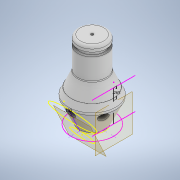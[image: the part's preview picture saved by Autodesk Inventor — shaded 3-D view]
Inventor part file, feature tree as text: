
AUTODESK INVENTOR PART (.ipt)
format: ipt  version: 2020 (Build 240168000, 168)  size: 301,056 bytes
history: native  units: in
note: dims shown in document units (in); Inventor stores cm internally (conversion verified against a paired STEP export)
features: sketch x6, hole x4, plane x2, fillet x2, revolve x1, pattern_circular x1
ambient origin geometry x8: Origin, YZ Plane, XZ Plane, XY Plane, X Axis, Y Axis, Z Axis, Center Point
bodies: Solid1 (feature_tree)
feature tree (16):
  revolve  "Revolution1"  [1 undecoded]
  hole  "Hole4"  [1 undecoded]
  hole  "Hole8"  [1 undecoded]
  sketch  "Sketch13"  dims[d2=90.0deg d3=0.057in]
  plane  "Work Plane6"
  sketch  "Sketch14"  dims[d4=0.095in d5=0.125in]
  sketch  "Sketch29"  dims[d24=0.4466in d25=0.125in]
  plane  "Work Plane5"
  sketch  "Sketch30"  dims[d54=0.3779in d72=0.3779in d83=0.75in d84=0.75in d85=0.0625in d86=0.75in d87=0.375in d88=0.25in d89=0.5635in d90=1.1in d91=0.8108in d92=0.2645in d121=0.196in d122=0.25in d123=0.375in d124=0.25in d125=0.5635in d126=0.25in d127=0.0in d137=0.3779in d155=0.3779in d173=0.3779in d191=0.3779in d221=0.3779in d239=0.3779in d253=0.4466in d254=0.1325in d255=0.0625in d256=0.25in d257=0.375in d258=0.25in d259=0.5635in d260=0.55in d261=0.0in d262=0.213in d263=0.25in d264=0.375in d265=0.25in d266=0.5635in d267=0.25in d268=0.0in d269=1.5748in d270=1.3743in d272=0.0625in d273=0.0625in]
  hole  "Hole9"  [1 undecoded]
  hole  "Hole10"  [1 undecoded]
  pattern_circular  "Circular Pattern7"  [2 undecoded]
  fillet  "Fillet1"  Radius=0.75in
  fillet  "Fillet2"  Radius=0.75in
  sketch  "Sketch12"  dims[d0=0.3328in d1=0.5in]
  sketch  "Sketch16"  dims[d6=90.0deg d23=0.65in]
note: 7 required parameter values undecoded (feature->parameter linkage not recoverable at this tier; creation-order binding heuristic only, values carry confidence <= 0.55)